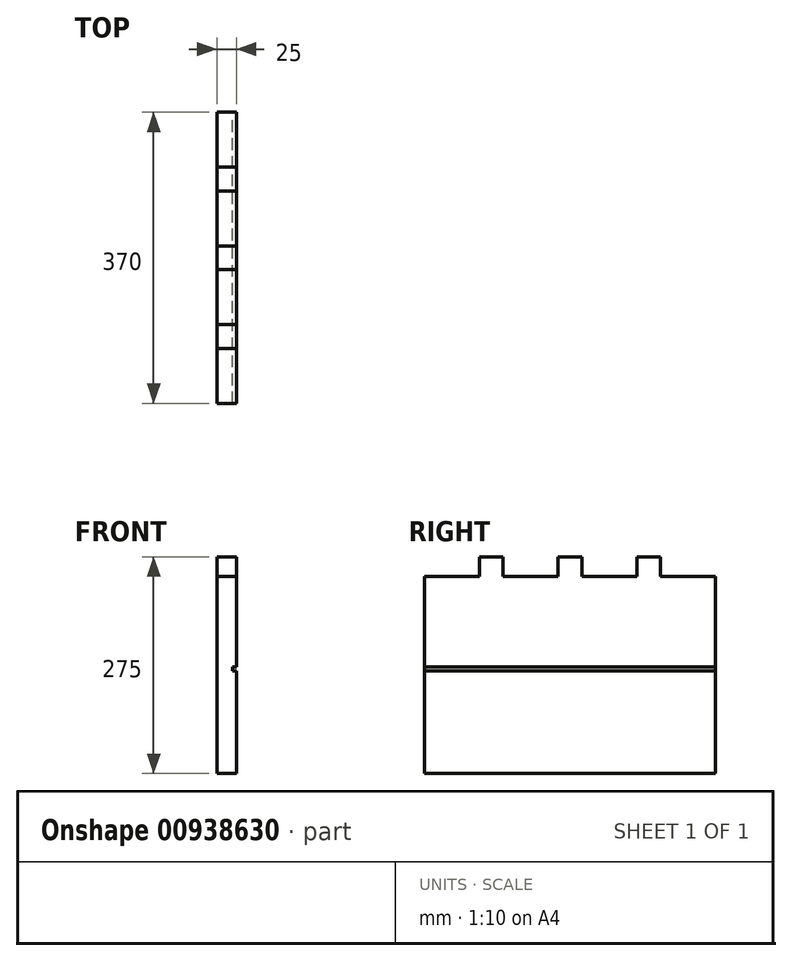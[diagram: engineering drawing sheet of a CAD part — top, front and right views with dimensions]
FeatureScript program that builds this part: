
annotation { "Feature Type Name" : "Feature", "Feature Type Description" : "" }
export const myFeature = defineFeature(function(context is Context, id is Id, definition is map)
    precondition{}
    {
        {
            var Q0;
            Q0=qCreatedBy(makeId("Right.planeOp"),FACE);
            var sketch = newSketch(context, id + "F0", { "sketchPlane" : qUnion([Q0])});
            skLineSegment(sketch, "E0.bottom", {"start": v(-183.38, 99.73) * mm, "end": v(186.62, 99.73) * mm});
            skLineSegment(sketch, "E0.top", {"start": v(-183.38, -150.27) * mm, "end": v(186.62, -150.27) * mm});
            skLineSegment(sketch, "E0.left", {"start": v(-183.38, 99.73) * mm, "end": v(-183.38, -150.27) * mm});
            skLineSegment(sketch, "E0.right", {"start": v(186.62, 99.73) * mm, "end": v(186.62, -150.27) * mm});
            skLineSegment(sketch, "E1.bottom", {"start": v(-113.38, 99.73) * mm, "end": v(-83.38, 99.73) * mm});
            skLineSegment(sketch, "E1.top", {"start": v(-113.38, 124.73) * mm, "end": v(-83.38, 124.73) * mm});
            skLineSegment(sketch, "E1.left", {"start": v(-113.38, 99.73) * mm, "end": v(-113.38, 124.73) * mm});
            skLineSegment(sketch, "E1.right", {"start": v(-83.38, 99.73) * mm, "end": v(-83.38, 124.73) * mm});
            skLineSegment(sketch, "E2.bottom", {"start": v(-13.38, 99.73) * mm, "end": v(16.62, 99.73) * mm});
            skLineSegment(sketch, "E2.top", {"start": v(-13.38, 124.73) * mm, "end": v(16.62, 124.73) * mm});
            skLineSegment(sketch, "E2.left", {"start": v(-13.38, 99.73) * mm, "end": v(-13.38, 124.73) * mm});
            skLineSegment(sketch, "E2.right", {"start": v(16.62, 99.73) * mm, "end": v(16.62, 124.73) * mm});
            skLineSegment(sketch, "E3.bottom", {"start": v(86.62, 99.73) * mm, "end": v(116.62, 99.73) * mm});
            skLineSegment(sketch, "E3.top", {"start": v(86.62, 124.73) * mm, "end": v(116.62, 124.73) * mm});
            skLineSegment(sketch, "E3.left", {"start": v(86.62, 99.73) * mm, "end": v(86.62, 124.73) * mm});
            skLineSegment(sketch, "E3.right", {"start": v(116.62, 99.73) * mm, "end": v(116.62, 124.73) * mm});
            skSolve(sketch);
        }
        {
            var Q0;
            Q0=qSketchRegion(id+"F0",true);
            extrude(context, id + "F1", {"entities" : qUnion([Q0]), "depth" : 25 * mm, "offsetDistance" : 25 * mm});
        }
        {
            var Q0;
            Q0=makeQuery(id+"F1.opExtrude","CAP_FACE",FACE,{"disambiguationData":[OSD([sQuery(id+"F0.wireOp",EDGE,"E0.bottom"),sQuery(id+"F0.wireOp",EDGE,"E0.top"),sQuery(id+"F0.wireOp",EDGE,"E0.left"),sQuery(id+"F0.wireOp",EDGE,"E0.right"),sQuery(id+"F0.wireOp",EDGE,"E1.top"),sQuery(id+"F0.wireOp",EDGE,"E1.left"),sQuery(id+"F0.wireOp",EDGE,"E1.right"),sQuery(id+"F0.wireOp",EDGE,"E2.top"),sQuery(id+"F0.wireOp",EDGE,"E2.left"),sQuery(id+"F0.wireOp",EDGE,"E2.right"),sQuery(id+"F0.wireOp",EDGE,"E3.top"),sQuery(id+"F0.wireOp",EDGE,"E3.left"),sQuery(id+"F0.wireOp",EDGE,"E3.right")])],"isStart":false});
            var sketch = newSketch(context, id + "F2", { "sketchPlane" : qUnion([Q0])});
            skLineSegment(sketch, "E4.bottom", {"start": v(-183.38, -15.27) * mm, "end": v(186.62, -15.27) * mm});
            skLineSegment(sketch, "E4.top", {"start": v(-183.38, -20.27) * mm, "end": v(186.62, -20.27) * mm});
            skLineSegment(sketch, "E4.left", {"start": v(-183.38, -15.27) * mm, "end": v(-183.38, -20.27) * mm});
            skLineSegment(sketch, "E4.right", {"start": v(186.62, -15.27) * mm, "end": v(186.62, -20.27) * mm});
            skSolve(sketch);
        }
        {
            var Q0;
            Q0=makeQuery(id+"F2.imprint","IMPRINT",FACE,{"disambiguationData":[TD([[makeQuery(id+"F2.imprint","IMPRINT",EDGE,{"derivedFrom":sQuery(id+"F2.wireOp",EDGE,"E4.bottom")}),-1.0]])]});
            extrude(context, id + "F3", {"entities" : qUnion([Q0]), "operationType" : NewBodyOperationType.REMOVE, "oppositeDirection" : true, "depth" : 5 * mm, "offsetDistance" : 25 * mm});
        }
    });
